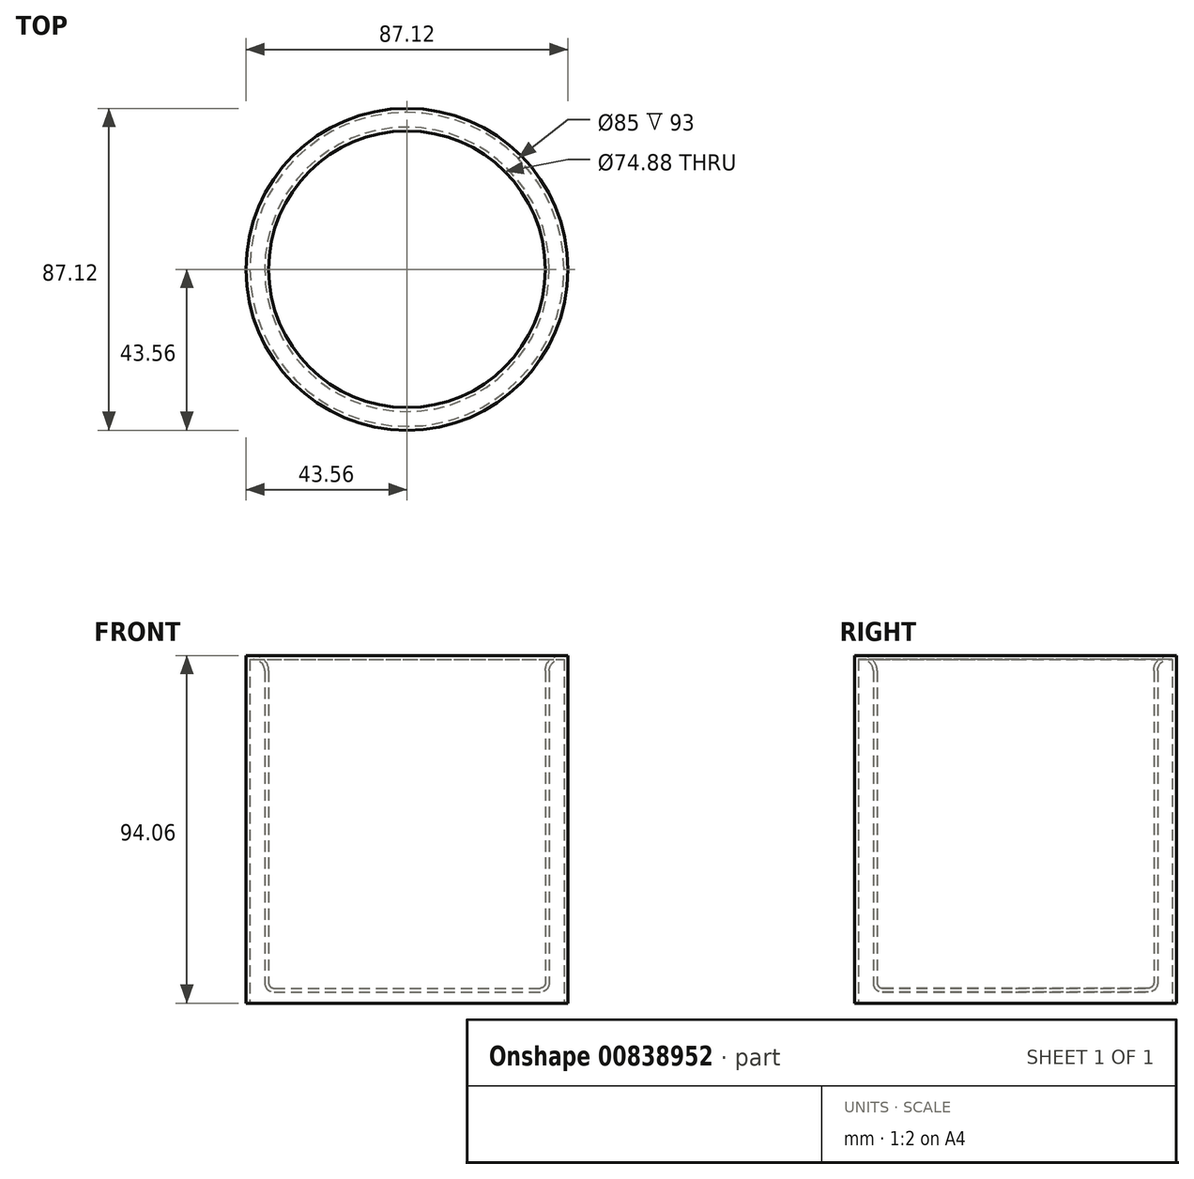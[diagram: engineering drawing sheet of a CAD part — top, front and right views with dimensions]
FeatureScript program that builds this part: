
annotation { "Feature Type Name" : "Feature", "Feature Type Description" : "" }
export const myFeature = defineFeature(function(context is Context, id is Id, definition is map)
    precondition{}
    {
        {
            var Q0;
            Q0=qCreatedBy(makeId("Front.planeOp"),FACE);
            var sketch = newSketch(context, id + "F0", { "sketchPlane" : qUnion([Q0])});
            skLineSegment(sketch, "E0", {"start": v(0, 0) * mm, "end": v(36, 0) * mm});
            skLineSegment(sketch, "E1", {"start": v(38.5, 2.5) * mm, "end": v(38.5, 87) * mm});
            skLineSegment(sketch, "E2", {"start": v(41.5, 90) * mm, "end": v(42.5, 90) * mm});
            skLineSegment(sketch, "E3", {"start": v(42.5, 90) * mm, "end": v(42.5, -3) * mm});
            skPoint(sketch, "E4.visualSharp", {"position": v(38.5, 90) * mm});
            skArc(sketch, "E4.filletArc", {"start": v(41.5, 90) * mm, "mid": v(39.38, 89.12) * mm, "end": v(38.5, 87) * mm});
            skLineSegment(sketch, "E5.4", {"start": v(40.44, 91.06) * mm, "end": v(42.5, 91.06) * mm});
            skPoint(sketch, "E6.visualSharp", {"position": v(38.5, 0) * mm});
            skArc(sketch, "E6.filletArc", {"start": v(36, 0) * mm, "mid": v(37.77, 0.73) * mm, "end": v(38.5, 2.5) * mm});
            skLineSegment(sketch, "E7.0", {"start": v(43.56, 91.06) * mm, "end": v(43.56, -3) * mm});
            skLineSegment(sketch, "E7.1", {"start": v(41.5, 91.06) * mm, "end": v(43.56, 91.06) * mm});
            skLineSegment(sketch, "E7.2", {"start": v(0, 1.06) * mm, "end": v(36, 1.06) * mm});
            skArc(sketch, "E7.3", {"start": v(36, 1.06) * mm, "mid": v(37.02, 1.48) * mm, "end": v(37.44, 2.5) * mm});
            skLineSegment(sketch, "E7.4", {"start": v(37.44, 2.5) * mm, "end": v(37.44, 87) * mm});
            skArc(sketch, "E7.5", {"start": v(41.5, 91.06) * mm, "mid": v(38.63, 89.87) * mm, "end": v(37.44, 87) * mm});
            skLineSegment(sketch, "E8", {"start": v(0, 0) * mm, "end": v(0, 1.06) * mm});
            skLineSegment(sketch, "E9", {"start": v(42.5, -3) * mm, "end": v(43.56, -3) * mm});
            skSolve(sketch);
        }
        {
            var Q0;
            Q0=makeQuery(id+"F0.imprint","IMPRINT",FACE,{"disambiguationData":[TD([[makeQuery(id+"F0.imprint","IMPRINT",EDGE,{"derivedFrom":sQuery(id+"F0.wireOp",EDGE,"E0")}),1.0]])]});
            var Q1;
            Q1=sQuery(id+"F0.wireOp",EDGE,"E8");
            revolve(context, id + "F1", {"entities" : qUnion([Q0]), "axis" : qUnion([Q1]), "revolveType" : RevolveType.FULL});
        }
    });
